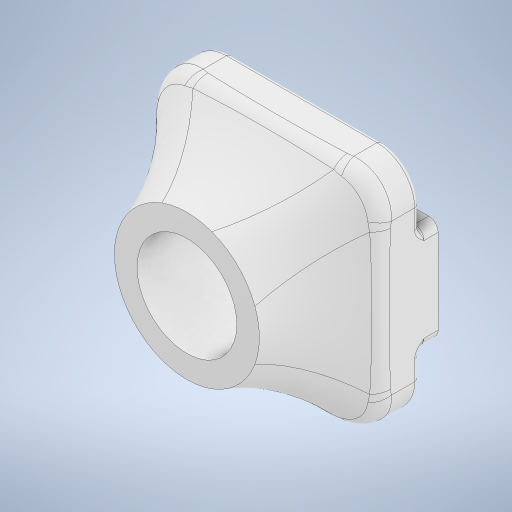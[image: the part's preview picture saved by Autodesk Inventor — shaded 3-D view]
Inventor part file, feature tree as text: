
AUTODESK INVENTOR PART (.ipt)
format: ipt  version: 2024 (Build 280153000, 153)  size: 556,544 bytes
history: native  units: mm
features: fillet x6, extrude x3, sketch x3, projected_geometry x2
ambient origin geometry x8: Origin, YZ Plane, XZ Plane, XY Plane, X Axis, Y Axis, Z Axis, Center Point
bodies: Solid1 (feature_tree)
feature tree (14):
  extrude  "Extrusion1"  Depth=1.2mm
  extrude  "Extrusion2"  Depth=12.0mm
  fillet  "Fillet1"  Radius=12.0mm
  fillet  "Fillet2"  Radius=2.0mm
  extrude  "Extrusion3"  Depth=8.0mm
  fillet  "Fillet3"  Radius=5.5mm
  fillet  "Fillet4"  Radius=1.0mm
  fillet  "Fillet5"  Radius=1.0mm
  fillet  "Fillet6"  Radius=0.5mm
  sketch  "Sketch1"  dims[d0=5.3mm d1=1.2mm]
  sketch  "Sketch2"  dims[d2=6.35mm d3=0.0mm d4=12.0mm d5=12.0mm d6=2.0mm d7=0.0mm]
  projected_geometry  "Projected Loop1"
  sketch  "Sketch3"  dims[d8=2.0mm d9=8.0mm d10=5.5mm d12=1.0mm d13=1.0mm d14=0.0mm d15=0.5mm d16=0.25mm d17=1.0mm d18=0.25mm]
  projected_geometry  "Projected Loop2"
